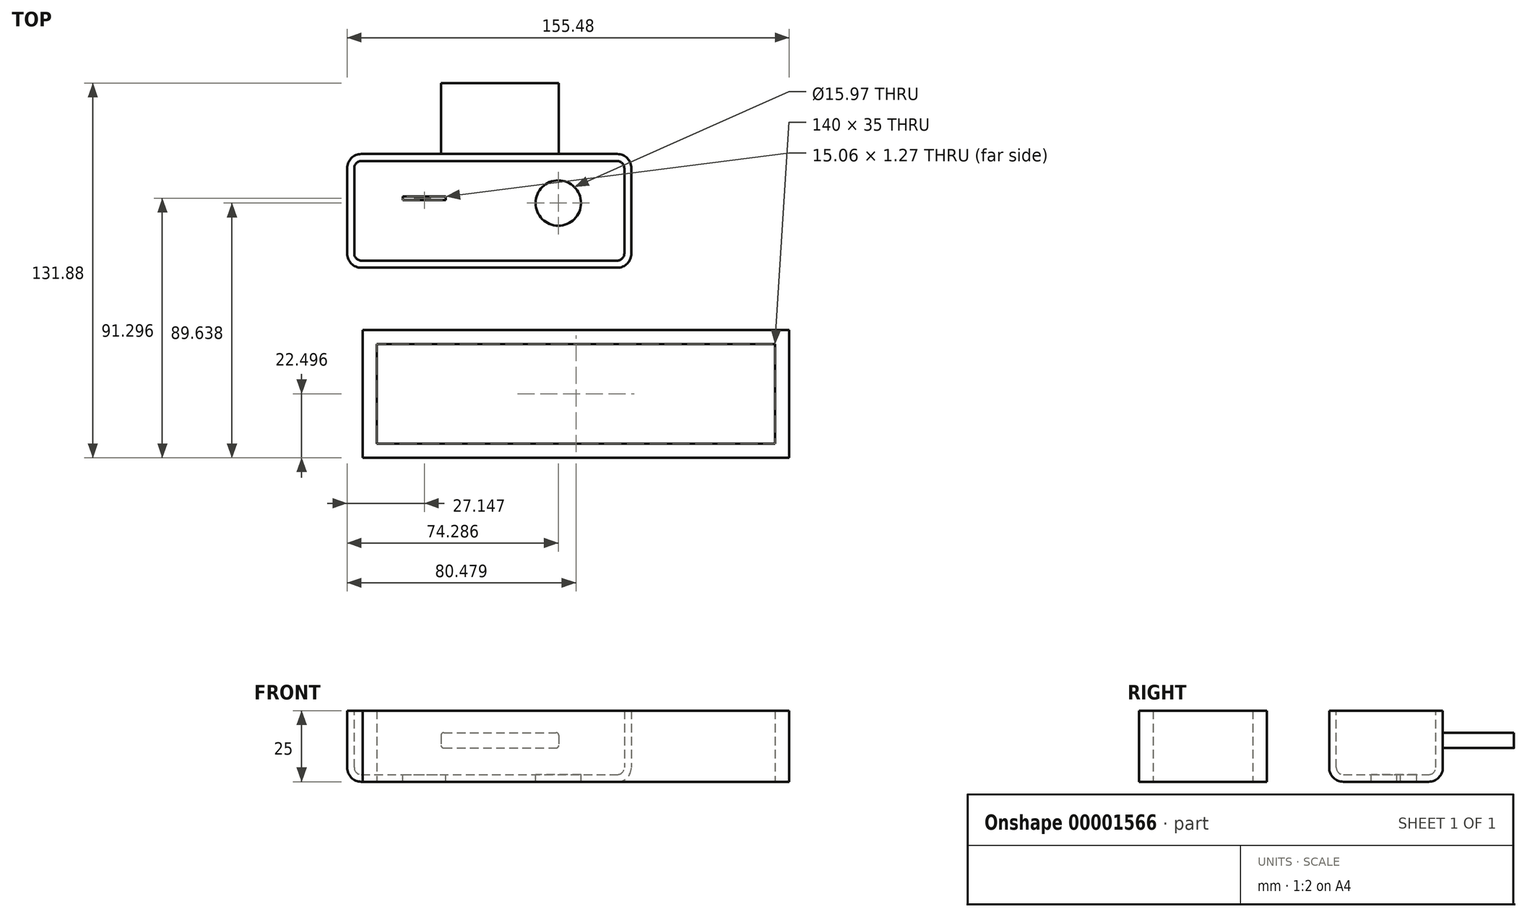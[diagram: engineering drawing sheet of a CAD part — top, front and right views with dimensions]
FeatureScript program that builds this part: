
annotation { "Feature Type Name" : "Feature", "Feature Type Description" : "" }
export const myFeature = defineFeature(function(context is Context, id is Id, definition is map)
    precondition{}
    {
        {
            var Q0;
            Q0=qCreatedBy(makeId("Top.planeOp"),FACE);
            var sketch = newSketch(context, id + "F0", { "sketchPlane" : qUnion([Q0])});
            skLineSegment(sketch, "E0", {"start": v(-59.9, -15.6) * mm, "end": v(-59.9, 24.4) * mm});
            skLineSegment(sketch, "E1", {"start": v(-59.9, 24.4) * mm, "end": v(40.1, 24.4) * mm});
            skLineSegment(sketch, "E2", {"start": v(40.1, 24.4) * mm, "end": v(40.1, -15.6) * mm});
            skLineSegment(sketch, "E3", {"start": v(40.1, -15.6) * mm, "end": v(-59.9, -15.6) * mm});
            skSolve(sketch);
        }
        {
            var Q0;
            Q0=makeQuery(id+"F0.imprint","IMPRINT",FACE,{"disambiguationData":[TD([[makeQuery(id+"F0.imprint","IMPRINT",EDGE,{"derivedFrom":sQuery(id+"F0.wireOp",EDGE,"E0")}),-1.0]])]});
            extrude(context, id + "F1", {"entities" : qUnion([Q0]), "depth" : 25 * mm});
        }
        {
            var Q0;
            Q0=makeQuery(id+"F1.opExtrude","SWEPT_EDGE",EDGE,{"disambiguationData":[OSD([sQuery(id+"F0.wireOp",EDGE,"E0"),sQuery(id+"F0.wireOp",EDGE,"E3")])]});
            var Q1;
            Q1=makeQuery(id+"F1.opExtrude","SWEPT_EDGE",EDGE,{"disambiguationData":[OSD([sQuery(id+"F0.wireOp",EDGE,"E2"),sQuery(id+"F0.wireOp",EDGE,"E3")])]});
            var Q2;
            Q2=makeQuery(id+"F1.opExtrude","SWEPT_EDGE",EDGE,{"disambiguationData":[OSD([sQuery(id+"F0.wireOp",EDGE,"E1"),sQuery(id+"F0.wireOp",EDGE,"E2")])]});
            var Q3;
            Q3=makeQuery(id+"F1.opExtrude","SWEPT_EDGE",EDGE,{"disambiguationData":[OSD([sQuery(id+"F0.wireOp",EDGE,"E0"),sQuery(id+"F0.wireOp",EDGE,"E1")])]});
            var Q4;
            Q4=makeQuery(id+"F1.opExtrude","CAP_FACE",FACE,{"disambiguationData":[OSD([sQuery(id+"F0.wireOp",EDGE,"E0"),sQuery(id+"F0.wireOp",EDGE,"E1"),sQuery(id+"F0.wireOp",EDGE,"E2"),sQuery(id+"F0.wireOp",EDGE,"E3")])],"isStart":true});
            fillet(context, id + "F2", {"entities" : qUnion([Q0, Q1, Q2, Q3, Q4]), "radius" : 5 * mm, "tangentPropagation" : true, "allowEdgeOverflow" : false});
        }
        {
            var Q0;
            Q0=makeQuery(id+"F1.opExtrude","CAP_FACE",FACE,{"disambiguationData":[OSD([sQuery(id+"F0.wireOp",EDGE,"E0"),sQuery(id+"F0.wireOp",EDGE,"E1"),sQuery(id+"F0.wireOp",EDGE,"E2"),sQuery(id+"F0.wireOp",EDGE,"E3")])],"isStart":false});
            shell(context, id + "F3", {"entities" : qUnion([Q0]), "thickness" : 2.5 * mm});
        }
        {
            var Q0;
            Q0=makeQuery(id+"F3.opShell","OFFSET_FACE",FACE,{"disambiguationData":[OSD([sQuery(id+"F0.wireOp",EDGE,"E0"),sQuery(id+"F0.wireOp",EDGE,"E1"),sQuery(id+"F0.wireOp",EDGE,"E2"),sQuery(id+"F0.wireOp",EDGE,"E3")])]});
            var sketch = newSketch(context, id + "F4", { "sketchPlane" : qUnion([Q0])});
            skCircle(sketch, "E4", {"center": v(14.39, 7.16) * mm, "radius": 7.99 * mm});
            skSolve(sketch);
        }
        {
            var Q0;
            Q0 = qSketchRegion(id + "F4", true);
            extrude(context, id + "F5", {"entities" : qUnion([Q0]), "operationType" : NewBodyOperationType.REMOVE, "endBound" : BoundingType.THROUGH_ALL, "oppositeDirection" : true, "depth" : 25 * mm});
        }
        {
            var Q0;
            Q0=makeQuery(id+"F3.opShell","OFFSET_FACE",FACE,{"disambiguationData":[OSD([sQuery(id+"F0.wireOp",EDGE,"E0"),sQuery(id+"F0.wireOp",EDGE,"E1"),sQuery(id+"F0.wireOp",EDGE,"E2"),sQuery(id+"F0.wireOp",EDGE,"E3")])]});
            var sketch = newSketch(context, id + "F6", { "sketchPlane" : qUnion([Q0])});
            skLineSegment(sketch, "E5.bottom", {"start": v(-40.29, 8.18) * mm, "end": v(-25.22, 8.18) * mm});
            skLineSegment(sketch, "E5.top", {"start": v(-40.29, 9.45) * mm, "end": v(-25.22, 9.45) * mm});
            skLineSegment(sketch, "E5.left", {"start": v(-40.29, 8.18) * mm, "end": v(-40.29, 9.45) * mm});
            skLineSegment(sketch, "E5.right", {"start": v(-25.22, 8.18) * mm, "end": v(-25.22, 9.45) * mm});
            skSolve(sketch);
        }
        {
            var Q0;
            Q0=makeQuery(id+"F6.imprint","IMPRINT",FACE,{"disambiguationData":[TD([[makeQuery(id+"F6.imprint","IMPRINT",EDGE,{"derivedFrom":sQuery(id+"F6.wireOp",EDGE,"E5.bottom")}),1.0]])]});
            extrude(context, id + "F7", {"entities" : qUnion([Q0]), "operationType" : NewBodyOperationType.REMOVE, "endBound" : BoundingType.THROUGH_ALL, "oppositeDirection" : true, "depth" : 25 * mm});
        }
        {
            var Q0;
            Q0=qCreatedBy(makeId("Top.planeOp"),FACE);
            var sketch = newSketch(context, id + "F8", { "sketchPlane" : qUnion([Q0])});
            skLineSegment(sketch, "E6.bottom", {"start": v(-54.42, -37.48) * mm, "end": v(95.58, -37.48) * mm});
            skLineSegment(sketch, "E6.top", {"start": v(-54.42, -82.48) * mm, "end": v(95.58, -82.48) * mm});
            skLineSegment(sketch, "E6.left", {"start": v(-54.42, -37.48) * mm, "end": v(-54.42, -82.48) * mm});
            skLineSegment(sketch, "E6.right", {"start": v(95.58, -37.48) * mm, "end": v(95.58, -82.48) * mm});
            skLineSegment(sketch, "E7.bottom", {"start": v(-49.42, -42.48) * mm, "end": v(90.58, -42.48) * mm});
            skLineSegment(sketch, "E7.top", {"start": v(-49.42, -77.48) * mm, "end": v(90.58, -77.48) * mm});
            skLineSegment(sketch, "E7.left", {"start": v(-49.42, -42.48) * mm, "end": v(-49.42, -77.48) * mm});
            skLineSegment(sketch, "E7.right", {"start": v(90.58, -42.48) * mm, "end": v(90.58, -77.48) * mm});
            skSolve(sketch);
        }
        {
            var Q0;
            Q0=makeQuery(id+"F8.imprint","IMPRINT",FACE,{"disambiguationData":[TD([[makeQuery(id+"F8.imprint","IMPRINT",EDGE,{"derivedFrom":sQuery(id+"F8.wireOp",EDGE,"E6.bottom")}),-1.0]])]});
            extrude(context, id + "F9", {"entities" : qUnion([Q0]), "depth" : 25 * mm});
        }
        {
            var Q0;
            Q0=makeQuery(id+"F1.opExtrude","SWEPT_FACE",FACE,{"disambiguationData":[OSD([sQuery(id+"F0.wireOp",EDGE,"E1")])]});
            var sketch = newSketch(context, id + "F10", { "sketchPlane" : qUnion([Q0])});
            skLineSegment(sketch, "E8.bottom", {"start": v(26.86, 17.28) * mm, "end": v(-14.55, 17.28) * mm});
            skLineSegment(sketch, "E8.top", {"start": v(26.86, 11.84) * mm, "end": v(-14.55, 11.84) * mm});
            skLineSegment(sketch, "E8.left", {"start": v(26.86, 17.28) * mm, "end": v(26.86, 11.84) * mm});
            skLineSegment(sketch, "E8.right", {"start": v(-14.55, 17.28) * mm, "end": v(-14.55, 11.84) * mm});
            skSolve(sketch);
        }
        {
            var Q0;
            Q0=makeQuery(id+"F10.imprint","IMPRINT",FACE,{"disambiguationData":[TD([[makeQuery(id+"F10.imprint","IMPRINT",EDGE,{"derivedFrom":sQuery(id+"F10.wireOp",EDGE,"E8.bottom")}),1.0]])]});
            extrude(context, id + "F11", {"entities" : qUnion([Q0]), "operationType" : NewBodyOperationType.ADD, "depth" : 25 * mm});
        }
        {
            var Q0;
            Q0=makeQuery(id+"F11.opExtrude","SWEPT_EDGE",EDGE,{"disambiguationData":[OSD([sQuery(id+"F10.wireOp",EDGE,"E8.bottom"),sQuery(id+"F10.wireOp",EDGE,"E8.right")])]});
            var Q1;
            Q1=makeQuery(id+"F11.opExtrude","SWEPT_EDGE",EDGE,{"disambiguationData":[OSD([sQuery(id+"F10.wireOp",EDGE,"E8.top"),sQuery(id+"F10.wireOp",EDGE,"E8.right")])]});
            var Q2;
            Q2=makeQuery(id+"F11.opExtrude","SWEPT_EDGE",EDGE,{"disambiguationData":[OSD([sQuery(id+"F10.wireOp",EDGE,"E8.bottom"),sQuery(id+"F10.wireOp",EDGE,"E8.left")])]});
            var Q3;
            Q3=makeQuery(id+"F11.opExtrude","SWEPT_EDGE",EDGE,{"disambiguationData":[OSD([sQuery(id+"F10.wireOp",EDGE,"E8.top"),sQuery(id+"F10.wireOp",EDGE,"E8.left")])]});
            var Q4;
            Q4=makeQuery(id+"F11.opExtrude","CAP_EDGE",EDGE,{"disambiguationData":[OSD([sQuery(id+"F10.wireOp",EDGE,"E8.top")])],"isStart":true});
            fillet(context, id + "F12", {"entities" : qUnion([Q0, Q1, Q2, Q3, Q4]), "radius" : 1 * mm, "tangentPropagation" : true, "allowEdgeOverflow" : false});
        }
    });
